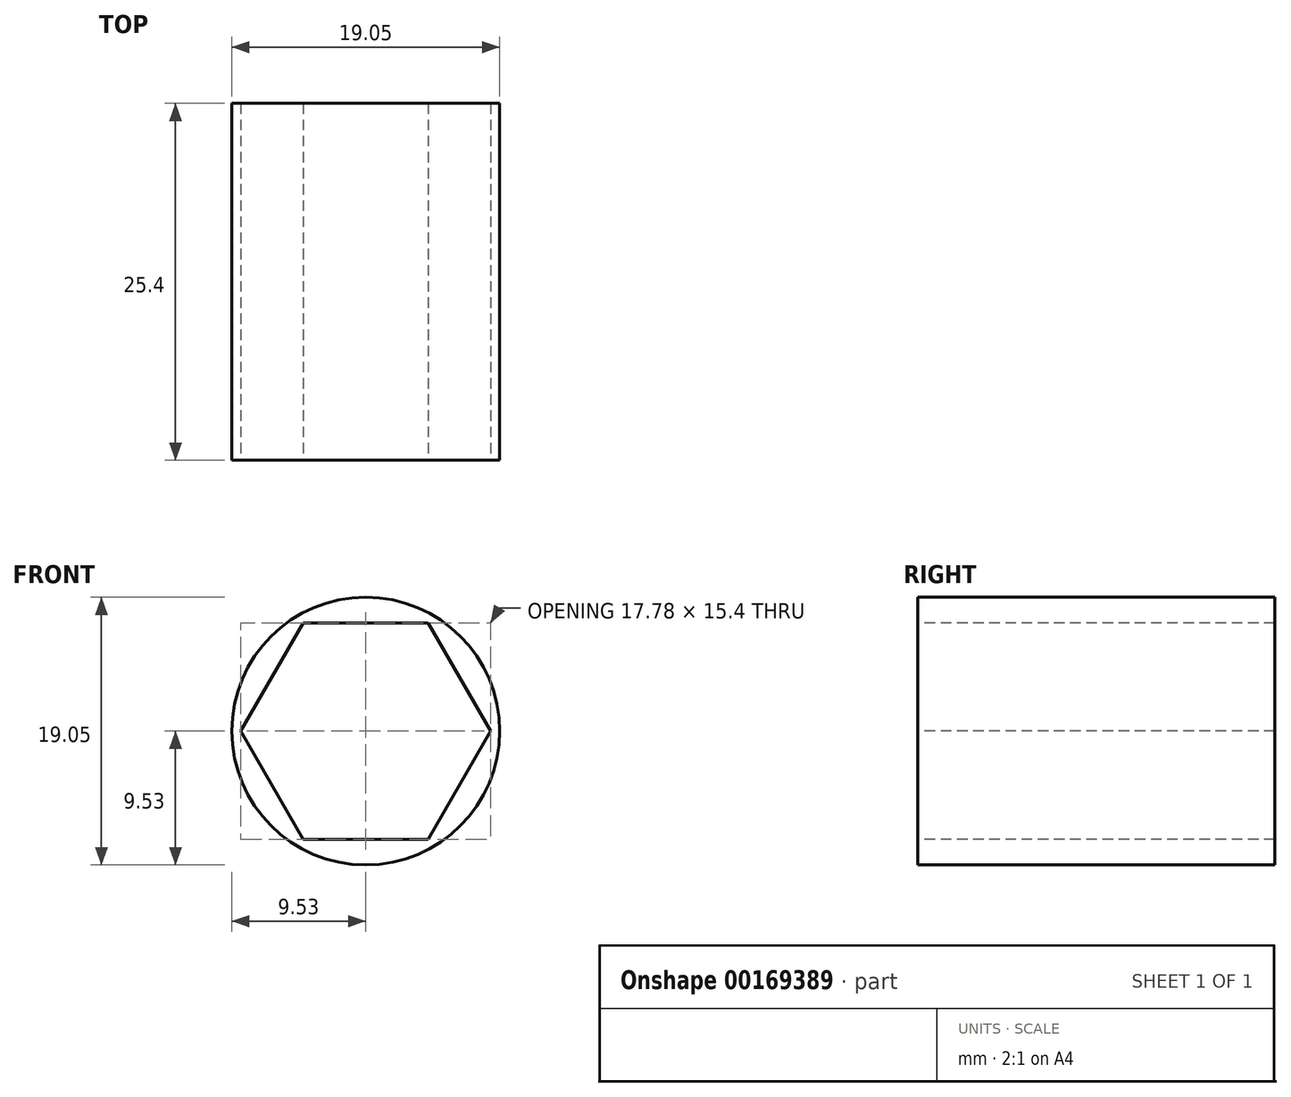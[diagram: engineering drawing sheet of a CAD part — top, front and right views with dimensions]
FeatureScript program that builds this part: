
annotation { "Feature Type Name" : "Feature", "Feature Type Description" : "" }
export const myFeature = defineFeature(function(context is Context, id is Id, definition is map)
    precondition{}
    {
        {
            var Q0;
            Q0=qCreatedBy(makeId("Front.planeOp"),FACE);
            var sketch = newSketch(context, id + "F0", { "sketchPlane" : qUnion([Q0])});
            skCircle(sketch, "E0", {"center": v(0, 0) * mm, "radius": 9.53 * mm});
            skSolve(sketch);
        }
        {
            var Q0;
            Q0 = qSketchRegion(id + "F0", true);
            extrude(context, id + "F1", {"entities" : qUnion([Q0]), "depth" : 25.4 * mm});
        }
        {
            var Q0;
            Q0=qCreatedBy(makeId("Front.planeOp"),FACE);
            var sketch = newSketch(context, id + "F2", { "sketchPlane" : qUnion([Q0])});
            skLineSegment(sketch, "E1.bottom", {"start": v(-4.84, 4.7) * mm, "end": v(4.69, 4.7) * mm});
            skLineSegment(sketch, "E1.top", {"start": v(-4.84, -4.82) * mm, "end": v(4.69, -4.82) * mm});
            skLineSegment(sketch, "E1.left", {"start": v(-4.84, 4.7) * mm, "end": v(-4.84, -4.82) * mm});
            skLineSegment(sketch, "E1.right", {"start": v(4.69, 4.7) * mm, "end": v(4.69, -4.82) * mm});
            skPoint(sketch, "E1.middle", {"position": v(-0.07, -0.06) * mm});
            skCircle(sketch, "E2", {"center": v(0, 0) * mm, "radius": 4.84 * mm});
            skSolve(sketch);
        }
        {
            var Q0;
            {var subQ0=sQuery(id+"F2.wireOp",EDGE,"E2");var subQ6=sQuery(id+"F2.wireOp",EDGE,"E1.bottom");var subQ9=makeQuery(id+"F2.imprint","INTERSECT",VERTEX,{"disambiguationData":[OD(0.0)],"derivedFrom":[subQ6,subQ0]});Q0=makeQuery(id+"F2.imprint","IMPRINT",FACE,{"disambiguationData":[TD([[makeQuery(id+"F2.imprint","IMPRINT",EDGE,{"disambiguationData":[TD([[subQ9,-1.0]])],"derivedFrom":subQ6}),-1.0]])]});}
            extrude(context, id + "F3", {"entities" : qUnion([Q0]), "operationType" : NewBodyOperationType.REMOVE, "endBound" : BoundingType.THROUGH_ALL, "depth" : 25.4 * mm});
        }
        {
            var Q0;
            Q0 = qSketchRegion(id + "F2", true);
            extrude(context, id + "F4", {"entities" : qUnion([Q0]), "operationType" : NewBodyOperationType.REMOVE, "depth" : 11.1 * mm});
        }
        {
            var Q0;
            Q0=makeQuery(id+"F1.opExtrude","CAP_FACE",FACE,{"disambiguationData":[OSD([sQuery(id+"F0.wireOp",EDGE,"E0")])],"isStart":false});
            var sketch = newSketch(context, id + "F5", { "sketchPlane" : qUnion([Q0])});
            skCircle(sketch, "E3.cCircle", {"center": v(0, 0) * mm, "radius": 7.7 * mm, "construction": true});
            skLineSegment(sketch, "E3.0", {"start": v(-4.44, 7.7) * mm, "end": v(4.44, 7.7) * mm});
            skLineSegment(sketch, "E3.1", {"start": v(4.44, 7.7) * mm, "end": v(8.9, 0) * mm});
            skLineSegment(sketch, "E3.2", {"start": v(8.89, 0) * mm, "end": v(4.45, -7.7) * mm});
            skLineSegment(sketch, "E3.3", {"start": v(4.45, -7.7) * mm, "end": v(-4.44, -7.7) * mm});
            skLineSegment(sketch, "E3.4", {"start": v(-4.44, -7.7) * mm, "end": v(-8.9, 0) * mm});
            skLineSegment(sketch, "E3.5", {"start": v(-8.89, 0) * mm, "end": v(-4.44, 7.7) * mm});
            skPoint(sketch, "E3.0.midPoint", {"position": v(0, 7.7) * mm});
            skSolve(sketch);
        }
        {
            var Q0;
            Q0=makeQuery(id+"F5.imprint","IMPRINT",FACE,{"disambiguationData":[TD([[makeQuery(id+"F5.imprint","IMPRINT",EDGE,{"derivedFrom":sQuery(id+"F5.wireOp",EDGE,"E3.0")}),-1.0]])]});
            extrude(context, id + "F6", {"entities" : qUnion([Q0]), "operationType" : NewBodyOperationType.REMOVE, "oppositeDirection" : true, "depth" : 25.4 * mm});
        }
    });
